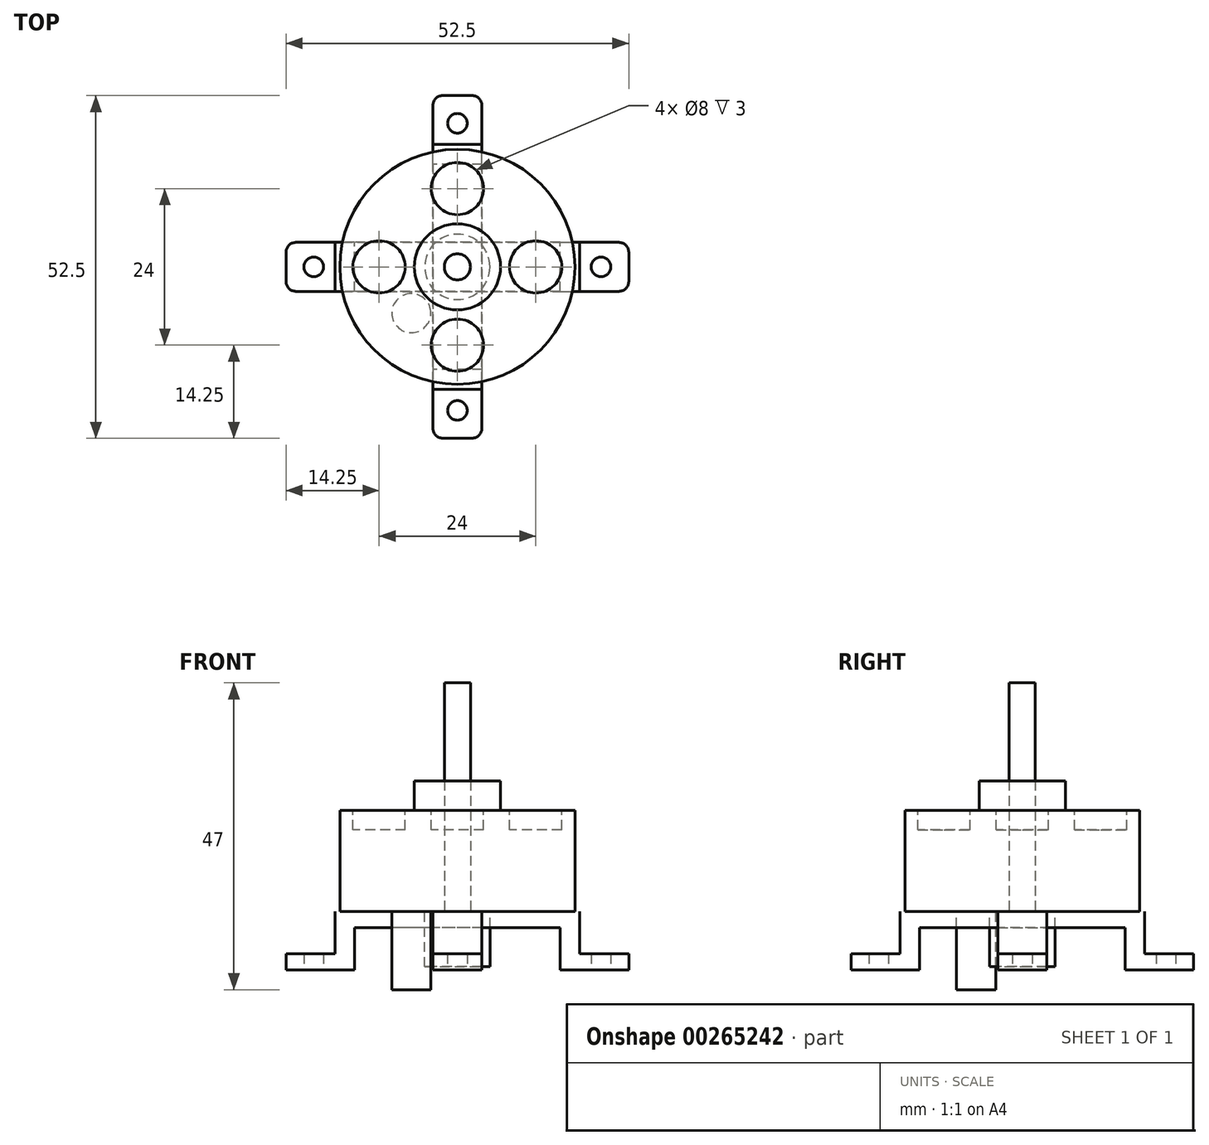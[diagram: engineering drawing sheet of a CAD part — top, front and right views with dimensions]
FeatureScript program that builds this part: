
annotation { "Feature Type Name" : "Feature", "Feature Type Description" : "" }
export const myFeature = defineFeature(function(context is Context, id is Id, definition is map)
    precondition{}
    {
        {
            var Q0;
            Q0=qCreatedBy(makeId("Right.planeOp"),FACE);
            var sketch = newSketch(context, id + "F0", { "sketchPlane" : qUnion([Q0])});
            skLineSegment(sketch, "E0", {"start": v(0, 6.5) * mm, "end": v(-15.75, 6.5) * mm});
            skLineSegment(sketch, "E1", {"start": v(-15.75, 6.5) * mm, "end": v(-15.75, 0) * mm});
            skLineSegment(sketch, "E2", {"start": v(-15.75, 0) * mm, "end": v(-26.25, 0) * mm});
            skLineSegment(sketch, "E3", {"start": v(-26.25, 0) * mm, "end": v(-26.25, 2.5) * mm});
            skLineSegment(sketch, "E4", {"start": v(-26.25, 2.5) * mm, "end": v(-18.75, 2.5) * mm});
            skLineSegment(sketch, "E5", {"start": v(-18.75, 2.5) * mm, "end": v(-18.75, 9) * mm});
            skLineSegment(sketch, "E6", {"start": v(-18.75, 9) * mm, "end": v(0, 9) * mm});
            skLineSegment(sketch, "E7", {"start": v(0, 9) * mm, "end": v(0, 6.5) * mm});
            skLineSegment(sketch, "E8", {"start": v(0, 0) * mm, "end": v(0, 30.17) * mm});
            skLineSegment(sketch, "E9.MirrorCS", {"start": v(26.25, 0) * mm, "end": v(26.25, 2.5) * mm});
            skLineSegment(sketch, "E10.MirrorCS", {"start": v(18.75, 2.5) * mm, "end": v(18.75, 9) * mm});
            skLineSegment(sketch, "E11.MirrorCS", {"start": v(26.25, 2.5) * mm, "end": v(18.75, 2.5) * mm});
            skLineSegment(sketch, "E12.MirrorCS", {"start": v(15.75, 0) * mm, "end": v(26.25, 0) * mm});
            skLineSegment(sketch, "E13.MirrorCS", {"start": v(15.75, 6.5) * mm, "end": v(15.75, 0) * mm});
            skLineSegment(sketch, "E14.MirrorCS", {"start": v(18.75, 9) * mm, "end": v(0, 9) * mm});
            skLineSegment(sketch, "E15.MirrorCS", {"start": v(0, 6.5) * mm, "end": v(15.75, 6.5) * mm});
            skSolve(sketch);
        }
        {
            var Q0;
            Q0 = qSketchRegion(id + "F0", true);
            extrude(context, id + "F1", {"entities" : qUnion([Q0]), "endBound" : BoundingType.SYMMETRIC, "depth" : 7.5 * mm});
        }
        {
            var Q0;
            Q0=makeQuery(id+"F1.opExtrude","SWEPT_FACE",FACE,{"disambiguationData":[OSD([sQuery(id+"F0.wireOp",EDGE,"E6")])]});
            var sketch = newSketch(context, id + "F2", { "sketchPlane" : qUnion([Q0])});
            skCircle(sketch, "E16", {"center": v(0, 0) * mm, "radius": 18 * mm});
            skCircle(sketch, "E17", {"center": v(0, 0) * mm, "radius": 2 * mm});
            skSolve(sketch);
        }
        {
            var Q0;
            Q0 = qSketchRegion(id + "F2", true);
            extrude(context, id + "F3", {"entities" : qUnion([Q0]), "depth" : 15.5 * mm});
        }
        {
            var Q0;
            Q0=makeQuery(id+"F3.opExtrude","CAP_FACE",FACE,{"disambiguationData":[OSD([sQuery(id+"F2.wireOp",EDGE,"E16"),sQuery(id+"F2.wireOp",EDGE,"E17")])],"isStart":false});
            var sketch = newSketch(context, id + "F4", { "sketchPlane" : qUnion([Q0])});
            skCircle(sketch, "E18", {"center": v(0, 0) * mm, "radius": 6.6 * mm});
            skCircle(sketch, "E19", {"center": v(0, 0) * mm, "radius": 2 * mm});
            skSolve(sketch);
        }
        {
            var Q0;
            Q0 = qSketchRegion(id + "F4", true);
            extrude(context, id + "F5", {"entities" : qUnion([Q0]), "operationType" : NewBodyOperationType.ADD, "depth" : 4.5 * mm});
        }
        {
            var Q0;
            Q0=makeQuery(id+"F3.opExtrude","CAP_FACE",FACE,{"disambiguationData":[OSD([sQuery(id+"F2.wireOp",EDGE,"E16"),sQuery(id+"F2.wireOp",EDGE,"E17")])],"isStart":true});
            var sketch = newSketch(context, id + "F6", { "sketchPlane" : qUnion([Q0])});
            skCircle(sketch, "E20", {"center": v(0, 0) * mm, "radius": 5 * mm});
            skSolve(sketch);
        }
        {
            var Q0;
            Q0 = qSketchRegion(id + "F6", true);
            extrude(context, id + "F7", {"entities" : qUnion([Q0]), "depth" : 8.5 * mm});
        }
        {
            var Q0;
            Q0=makeQuery(id+"F7.opExtrude","CAP_FACE",FACE,{"disambiguationData":[OSD([sQuery(id+"F6.wireOp",EDGE,"E20")])],"isStart":true});
            var sketch = newSketch(context, id + "F8", { "sketchPlane" : qUnion([Q0])});
            skCircle(sketch, "E21", {"center": v(0, 0) * mm, "radius": 2 * mm});
            skSolve(sketch);
        }
        {
            var Q0;
            Q0 = qSketchRegion(id + "F8", true);
            extrude(context, id + "F9", {"entities" : qUnion([Q0]), "depth" : 35 * mm});
        }
        {
            var Q0;
            Q0=makeQuery(id+"F3.opExtrude","CAP_FACE",FACE,{"disambiguationData":[OSD([sQuery(id+"F2.wireOp",EDGE,"E16"),sQuery(id+"F2.wireOp",EDGE,"E17")])],"isStart":false});
            var sketch = newSketch(context, id + "F10", { "sketchPlane" : qUnion([Q0])});
            skCircle(sketch, "E22", {"center": v(-12, 0) * mm, "radius": 4 * mm});
            skCircle(sketch, "E23", {"center": v(0, -12) * mm, "radius": 4 * mm});
            skCircle(sketch, "E24", {"center": v(0, 12) * mm, "radius": 4 * mm});
            skCircle(sketch, "E25", {"center": v(12, 0) * mm, "radius": 4 * mm});
            skSolve(sketch);
        }
        {
            var Q0;
            Q0 = qSketchRegion(id + "F10", true);
            extrude(context, id + "F11", {"entities" : qUnion([Q0]), "operationType" : NewBodyOperationType.REMOVE, "oppositeDirection" : true, "depth" : 3 * mm});
        }
        {
            var Q0;
            Q0=makeQuery(id+"F1.opExtrude","SWEPT_BODY",BODY,{"disambiguationData":[OSD([sQuery(id+"F0.wireOp",EDGE,"E0"),sQuery(id+"F0.wireOp",EDGE,"E1"),sQuery(id+"F0.wireOp",EDGE,"E2"),sQuery(id+"F0.wireOp",EDGE,"E3"),sQuery(id+"F0.wireOp",EDGE,"E4"),sQuery(id+"F0.wireOp",EDGE,"E5"),sQuery(id+"F0.wireOp",EDGE,"E6"),sQuery(id+"F0.wireOp",EDGE,"E9.MirrorCS"),sQuery(id+"F0.wireOp",EDGE,"E10.MirrorCS"),sQuery(id+"F0.wireOp",EDGE,"E11.MirrorCS"),sQuery(id+"F0.wireOp",EDGE,"E12.MirrorCS"),sQuery(id+"F0.wireOp",EDGE,"E13.MirrorCS"),sQuery(id+"F0.wireOp",EDGE,"E14.MirrorCS"),sQuery(id+"F0.wireOp",EDGE,"E15.MirrorCS")])]});
            var Q1;
            Q1=makeQuery(id+"F9.opExtrude","SWEPT_FACE",FACE,{"disambiguationData":[OSD([sQuery(id+"F8.wireOp",EDGE,"E21")])]});
            transform(context, id + "F12", {"entities" : qUnion([Q0]), "transformType" : TransformType.ROTATION, "transformAxis" : qUnion([Q1]), "angle" : 90 * degree, "makeCopy" : true});
        }
        {
            var Q0;
            Q0=makeQuery(id+"F1.opExtrude","CAP_EDGE",EDGE,{"disambiguationData":[OSD([sQuery(id+"F0.wireOp",EDGE,"E9.MirrorCS")])],"isStart":false});
            var Q1;
            Q1=makeQuery(id+"F1.opExtrude","CAP_EDGE",EDGE,{"disambiguationData":[OSD([sQuery(id+"F0.wireOp",EDGE,"E9.MirrorCS")])],"isStart":true});
            var Q2;
            Q2=makeQuery(id+"F12.opPattern","COPY",EDGE,{"derivedFrom":makeQuery(id+"F1.opExtrude","CAP_EDGE",EDGE,{"disambiguationData":[OSD([sQuery(id+"F0.wireOp",EDGE,"E9.MirrorCS")])],"isStart":true}),"instanceName":"1"});
            var Q3;
            Q3=makeQuery(id+"F12.opPattern","COPY",EDGE,{"derivedFrom":makeQuery(id+"F1.opExtrude","CAP_EDGE",EDGE,{"disambiguationData":[OSD([sQuery(id+"F0.wireOp",EDGE,"E9.MirrorCS")])],"isStart":false}),"instanceName":"1"});
            var Q4;
            Q4=makeQuery(id+"F1.opExtrude","CAP_EDGE",EDGE,{"disambiguationData":[OSD([sQuery(id+"F0.wireOp",EDGE,"E3")])],"isStart":false});
            var Q5;
            Q5=makeQuery(id+"F1.opExtrude","CAP_EDGE",EDGE,{"disambiguationData":[OSD([sQuery(id+"F0.wireOp",EDGE,"E3")])],"isStart":true});
            var Q6;
            Q6=makeQuery(id+"F12.opPattern","COPY",EDGE,{"derivedFrom":makeQuery(id+"F1.opExtrude","CAP_EDGE",EDGE,{"disambiguationData":[OSD([sQuery(id+"F0.wireOp",EDGE,"E3")])],"isStart":false}),"instanceName":"1"});
            var Q7;
            Q7=makeQuery(id+"F12.opPattern","COPY",EDGE,{"derivedFrom":makeQuery(id+"F1.opExtrude","CAP_EDGE",EDGE,{"disambiguationData":[OSD([sQuery(id+"F0.wireOp",EDGE,"E3")])],"isStart":true}),"instanceName":"1"});
            fillet(context, id + "F13", {"entities" : qUnion([Q0, Q1, Q2, Q3, Q4, Q5, Q6, Q7]), "radius" : 1.5 * mm, "tangentPropagation" : true, "allowEdgeOverflow" : false});
        }
        {
            var Q0;
            Q0=makeQuery(id+"F3.opExtrude","CAP_FACE",FACE,{"disambiguationData":[OSD([sQuery(id+"F2.wireOp",EDGE,"E16"),sQuery(id+"F2.wireOp",EDGE,"E17")])],"isStart":true});
            var sketch = newSketch(context, id + "F14", { "sketchPlane" : qUnion([Q0])});
            skCircle(sketch, "E26", {"center": v(-7.06, 7.09) * mm, "radius": 3 * mm});
            skSolve(sketch);
        }
        {
            var Q0;
            Q0 = qSketchRegion(id + "F14", true);
            extrude(context, id + "F15", {"entities" : qUnion([Q0]), "operationType" : NewBodyOperationType.ADD, "depth" : 12 * mm});
        }
        {
            var Q0;
            Q0=makeQuery(id+"F12.opPattern","COPY",FACE,{"derivedFrom":makeQuery(id+"F1.opExtrude","SWEPT_FACE",FACE,{"disambiguationData":[OSD([sQuery(id+"F0.wireOp",EDGE,"E2")])]}),"instanceName":"1"});
            var sketch = newSketch(context, id + "F16", { "sketchPlane" : qUnion([Q0])});
            skCircle(sketch, "E27", {"center": v(-22, 0) * mm, "radius": 1.5 * mm});
            skLineSegment(sketch, "E28", {"start": v(0, 0) * mm, "end": v(0, 48.25) * mm});
            skLineSegment(sketch, "E29", {"start": v(0, -28.98) * mm, "end": v(0, 48.25) * mm});
            skCircle(sketch, "E30.MirrorC", {"center": v(22, 0) * mm, "radius": 1.5 * mm});
            skSolve(sketch);
        }
        {
            var Q0;
            Q0 = qSketchRegion(id + "F16", true);
            extrude(context, id + "F17", {"entities" : qUnion([Q0]), "operationType" : NewBodyOperationType.REMOVE, "oppositeDirection" : true, "depth" : 25 * mm});
        }
        {
            var Q0;
            Q0=makeQuery(id+"F12.opPattern","COPY",BODY,{"derivedFrom":makeQuery(id+"F1.opExtrude","SWEPT_BODY",BODY,{"disambiguationData":[OSD([sQuery(id+"F0.wireOp",EDGE,"E0"),sQuery(id+"F0.wireOp",EDGE,"E1"),sQuery(id+"F0.wireOp",EDGE,"E2"),sQuery(id+"F0.wireOp",EDGE,"E3"),sQuery(id+"F0.wireOp",EDGE,"E4"),sQuery(id+"F0.wireOp",EDGE,"E5"),sQuery(id+"F0.wireOp",EDGE,"E6"),sQuery(id+"F0.wireOp",EDGE,"E9.MirrorCS"),sQuery(id+"F0.wireOp",EDGE,"E10.MirrorCS"),sQuery(id+"F0.wireOp",EDGE,"E11.MirrorCS"),sQuery(id+"F0.wireOp",EDGE,"E12.MirrorCS"),sQuery(id+"F0.wireOp",EDGE,"E13.MirrorCS"),sQuery(id+"F0.wireOp",EDGE,"E14.MirrorCS"),sQuery(id+"F0.wireOp",EDGE,"E15.MirrorCS")])]}),"instanceName":"1"});
            deleteBodies(context, id + "F18", {"entities" : qUnion([Q0])});
        }
        {
            var Q0;
            Q0=makeQuery(id+"F1.opExtrude","SWEPT_BODY",BODY,{"disambiguationData":[OSD([sQuery(id+"F0.wireOp",EDGE,"E0"),sQuery(id+"F0.wireOp",EDGE,"E1"),sQuery(id+"F0.wireOp",EDGE,"E2"),sQuery(id+"F0.wireOp",EDGE,"E3"),sQuery(id+"F0.wireOp",EDGE,"E4"),sQuery(id+"F0.wireOp",EDGE,"E5"),sQuery(id+"F0.wireOp",EDGE,"E6"),sQuery(id+"F0.wireOp",EDGE,"E9.MirrorCS"),sQuery(id+"F0.wireOp",EDGE,"E10.MirrorCS"),sQuery(id+"F0.wireOp",EDGE,"E11.MirrorCS"),sQuery(id+"F0.wireOp",EDGE,"E12.MirrorCS"),sQuery(id+"F0.wireOp",EDGE,"E13.MirrorCS"),sQuery(id+"F0.wireOp",EDGE,"E14.MirrorCS"),sQuery(id+"F0.wireOp",EDGE,"E15.MirrorCS")])]});
            var Q1;
            Q1=makeQuery(id+"F9.opExtrude","SWEPT_FACE",FACE,{"disambiguationData":[OSD([sQuery(id+"F8.wireOp",EDGE,"E21")])]});
            transform(context, id + "F19", {"entities" : qUnion([Q0]), "transformType" : TransformType.ROTATION, "transformAxis" : qUnion([Q1]), "angle" : 90 * degree, "makeCopy" : true});
        }
        {
            var Q0;
            Q0=qCreatedBy(makeId("Top.planeOp"),FACE);
            var sketch = newSketch(context, id + "F20", { "sketchPlane" : qUnion([Q0])});
            skCircle(sketch, "E31", {"center": v(0, 22) * mm, "radius": 1.5 * mm});
            skCircle(sketch, "E32", {"center": v(-22, 0) * mm, "radius": 1.5 * mm});
            skCircle(sketch, "E33", {"center": v(0, -22) * mm, "radius": 1.5 * mm});
            skCircle(sketch, "E34", {"center": v(22, 0) * mm, "radius": 1.5 * mm});
            skSolve(sketch);
        }
        {
            var Q0;
            Q0=sQuery(id+"F20.wireOp",VERTEX,"E32.center");
            var Q1;
            Q1=sQuery(id+"F20.wireOp",VERTEX,"E31.center");
            var Q2;
            Q2=sQuery(id+"F20.wireOp",VERTEX,"E33.center");
            var Q3;
            Q3=sQuery(id+"F20.wireOp",VERTEX,"E34.center");
            var Q4;
            Q4=makeQuery(id+"F1.opExtrude","SWEPT_BODY",BODY,{"disambiguationData":[OSD([sQuery(id+"F0.wireOp",EDGE,"E0"),sQuery(id+"F0.wireOp",EDGE,"E1"),sQuery(id+"F0.wireOp",EDGE,"E2"),sQuery(id+"F0.wireOp",EDGE,"E3"),sQuery(id+"F0.wireOp",EDGE,"E4"),sQuery(id+"F0.wireOp",EDGE,"E5"),sQuery(id+"F0.wireOp",EDGE,"E6"),sQuery(id+"F0.wireOp",EDGE,"E9.MirrorCS"),sQuery(id+"F0.wireOp",EDGE,"E10.MirrorCS"),sQuery(id+"F0.wireOp",EDGE,"E11.MirrorCS"),sQuery(id+"F0.wireOp",EDGE,"E12.MirrorCS"),sQuery(id+"F0.wireOp",EDGE,"E13.MirrorCS"),sQuery(id+"F0.wireOp",EDGE,"E14.MirrorCS"),sQuery(id+"F0.wireOp",EDGE,"E15.MirrorCS")])]});
            var Q5;
            Q5=makeQuery(id+"F19.opPattern","COPY",BODY,{"derivedFrom":makeQuery(id+"F1.opExtrude","SWEPT_BODY",BODY,{"disambiguationData":[OSD([sQuery(id+"F0.wireOp",EDGE,"E0"),sQuery(id+"F0.wireOp",EDGE,"E1"),sQuery(id+"F0.wireOp",EDGE,"E2"),sQuery(id+"F0.wireOp",EDGE,"E3"),sQuery(id+"F0.wireOp",EDGE,"E4"),sQuery(id+"F0.wireOp",EDGE,"E5"),sQuery(id+"F0.wireOp",EDGE,"E6"),sQuery(id+"F0.wireOp",EDGE,"E9.MirrorCS"),sQuery(id+"F0.wireOp",EDGE,"E10.MirrorCS"),sQuery(id+"F0.wireOp",EDGE,"E11.MirrorCS"),sQuery(id+"F0.wireOp",EDGE,"E12.MirrorCS"),sQuery(id+"F0.wireOp",EDGE,"E13.MirrorCS"),sQuery(id+"F0.wireOp",EDGE,"E14.MirrorCS"),sQuery(id+"F0.wireOp",EDGE,"E15.MirrorCS")])]}),"instanceName":"1"});
            hole(context, id + "F21", {"style" : HoleStyle.SIMPLE, "endStyle" : HoleEndStyle.THROUGH, "oppositeDirection" : true, "holeDiameter" : 3 * mm, "tappedDepth" : 12 * mm, "tapClearance" : 3, "locations" : qUnion([Q0, Q1, Q2, Q3]), "scope" : qUnion([Q4, Q5])});
        }
    });
